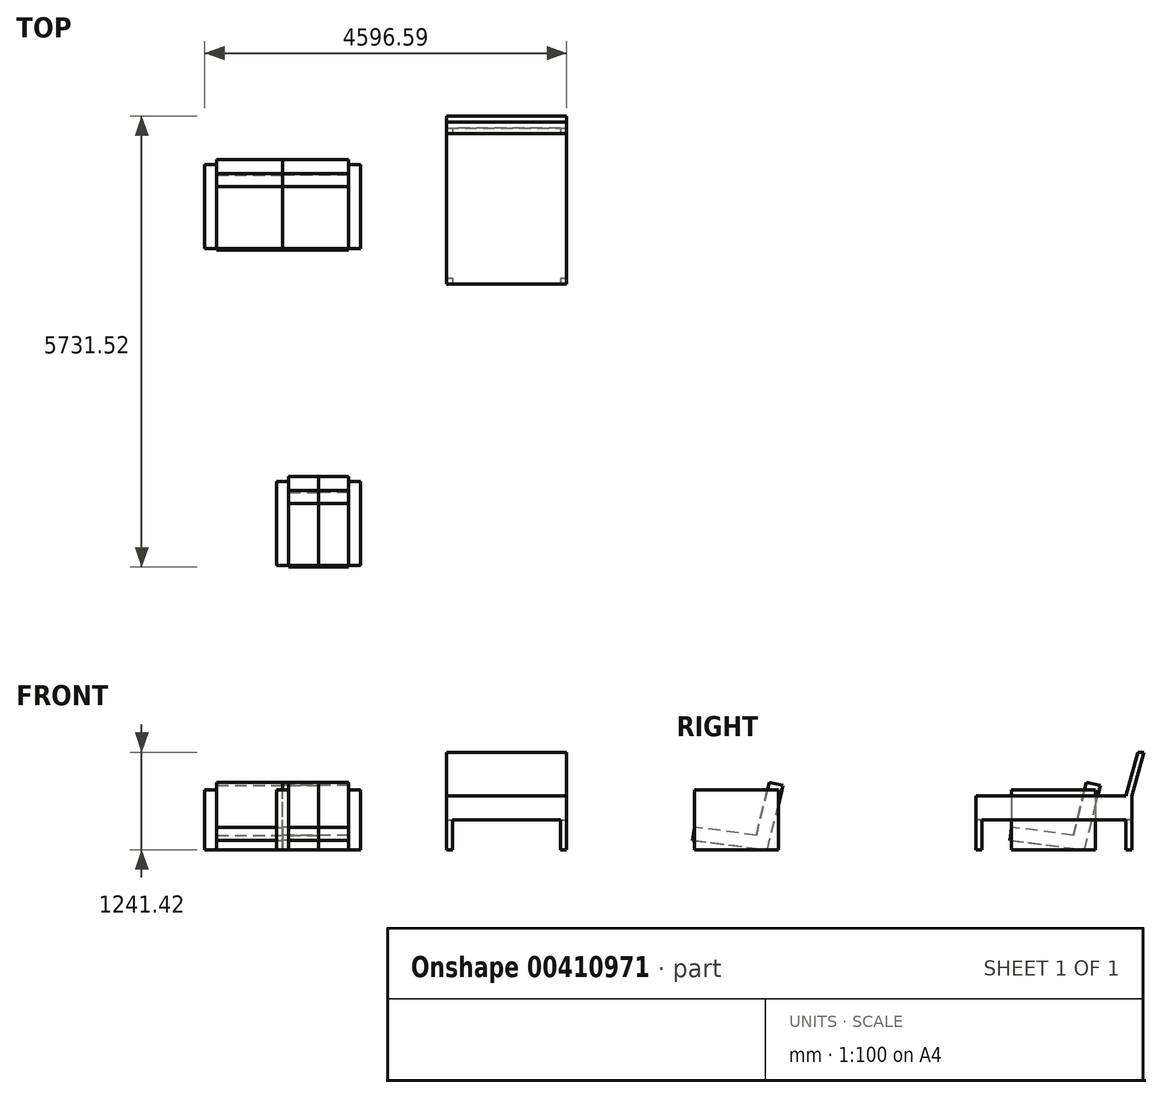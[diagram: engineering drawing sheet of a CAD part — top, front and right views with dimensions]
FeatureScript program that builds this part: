
annotation { "Feature Type Name" : "Feature", "Feature Type Description" : "" }
export const myFeature = defineFeature(function(context is Context, id is Id, definition is map)
    precondition{}
    {
        {
            var Q0;
            Q0=qCreatedBy(makeId("Top.planeOp"),FACE);
            var sketch = newSketch(context, id + "F0", { "sketchPlane" : qUnion([Q0])});
            skLineSegment(sketch, "E0.bottom", {"start": v(0, 0) * mm, "end": v(1524, 0) * mm});
            skLineSegment(sketch, "E0.top", {"start": v(0, 1981.2) * mm, "end": v(1524, 1981.2) * mm});
            skLineSegment(sketch, "E0.left", {"start": v(0, 0) * mm, "end": v(0, 1981.2) * mm});
            skLineSegment(sketch, "E0.right", {"start": v(1524, 0) * mm, "end": v(1524, 1981.2) * mm});
            skSolve(sketch);
        }
        {
            var Q0;
            Q0=makeQuery(id+"F0.imprint","IMPRINT",FACE,{"disambiguationData":[TD([[makeQuery(id+"F0.imprint","IMPRINT",EDGE,{"derivedFrom":sQuery(id+"F0.wireOp",EDGE,"E0.bottom")}),1.0]])]});
            extrude(context, id + "F1", {"entities" : qUnion([Q0]), "depth" : 685.8 * mm});
        }
        {
            var Q0;
            Q0=makeQuery(id+"F1.opExtrude","SWEPT_FACE",FACE,{"disambiguationData":[OSD([sQuery(id+"F0.wireOp",EDGE,"E0.bottom")])]});
            var sketch = newSketch(context, id + "F2", { "sketchPlane" : qUnion([Q0])});
            skLineSegment(sketch, "E1", {"start": v(0, 0) * mm, "end": v(76.2, 0) * mm});
            skLineSegment(sketch, "E2", {"start": v(76.2, 0) * mm, "end": v(76.2, 381) * mm});
            skLineSegment(sketch, "E3", {"start": v(76.2, 381) * mm, "end": v(1447.8, 381) * mm});
            skLineSegment(sketch, "E4", {"start": v(1447.8, 381) * mm, "end": v(1447.8, 0) * mm});
            skLineSegment(sketch, "E5", {"start": v(1447.8, 0) * mm, "end": v(1524, 0) * mm});
            skSolve(sketch);
        }
        {
            var Q0;
            {var subQ0=sQuery(id+"F2.wireOp",EDGE,"E2");Q0=makeQuery(id+"F2.imprint","IMPRINT",FACE,{"disambiguationData":[TD([[makeQuery(id+"F2.imprint","IMPRINT",EDGE,{"derivedFrom":subQ0}),-1.0]])]});}
            extrude(context, id + "F3", {"entities" : qUnion([Q0]), "operationType" : NewBodyOperationType.REMOVE, "endBound" : BoundingType.THROUGH_ALL, "oppositeDirection" : true, "depth" : 30.48 * mm});
        }
        {
            var Q0;
            Q0=makeQuery(id+"F1.opExtrude","SWEPT_FACE",FACE,{"disambiguationData":[OSD([sQuery(id+"F0.wireOp",EDGE,"E0.right")])]});
            var sketch = newSketch(context, id + "F4", { "sketchPlane" : qUnion([Q0])});
            skLineSegment(sketch, "E6", {"start": v(0, 0) * mm, "end": v(76.2, 0) * mm});
            skLineSegment(sketch, "E7", {"start": v(76.2, 0) * mm, "end": v(76.2, 381) * mm});
            skLineSegment(sketch, "E8", {"start": v(76.2, 381) * mm, "end": v(1905, 381) * mm});
            skLineSegment(sketch, "E9", {"start": v(1905, 381) * mm, "end": v(1905, 0) * mm});
            skLineSegment(sketch, "E10", {"start": v(1905, 0) * mm, "end": v(1981.2, 0) * mm});
            skSolve(sketch);
        }
        {
            var Q0;
            {var subQ0=sQuery(id+"F4.wireOp",EDGE,"E7");Q0=makeQuery(id+"F4.imprint","IMPRINT",FACE,{"disambiguationData":[TD([[makeQuery(id+"F4.imprint","IMPRINT",EDGE,{"derivedFrom":subQ0}),-1.0]])]});}
            extrude(context, id + "F5", {"entities" : qUnion([Q0]), "operationType" : NewBodyOperationType.REMOVE, "endBound" : BoundingType.THROUGH_ALL, "oppositeDirection" : true, "depth" : 30.48 * mm});
        }
        {
            var Q0;
            Q0=makeQuery(id+"F1.opExtrude","SWEPT_FACE",FACE,{"disambiguationData":[OSD([sQuery(id+"F0.wireOp",EDGE,"E0.right")])]});
            var sketch = newSketch(context, id + "F6", { "sketchPlane" : qUnion([Q0])});
            skLineSegment(sketch, "E11", {"start": v(1981.2, 685.8) * mm, "end": v(1906.52, 685.8) * mm});
            skLineSegment(sketch, "E12", {"start": v(1906.52, 685.8) * mm, "end": v(2057.29, 1241.42) * mm});
            skLineSegment(sketch, "E13", {"start": v(2057.29, 1241.42) * mm, "end": v(2131.97, 1241.42) * mm});
            skLineSegment(sketch, "E14", {"start": v(2131.97, 1241.42) * mm, "end": v(1981.2, 685.8) * mm});
            skSolve(sketch);
        }
        {
            var Q0;
            Q0=makeQuery(id+"F6.imprint","IMPRINT",FACE,{"disambiguationData":[TD([[makeQuery(id+"F6.imprint","IMPRINT",EDGE,{"derivedFrom":sQuery(id+"F6.wireOp",EDGE,"E11")}),1.0]])]});
            var Q1;
            Q1=makeQuery(id+"F1.opExtrude","SWEPT_FACE",FACE,{"disambiguationData":[OSD([sQuery(id+"F0.wireOp",EDGE,"E0.left")])]});
            extrude(context, id + "F7", {"entities" : qUnion([Q0]), "operationType" : NewBodyOperationType.ADD, "endBound" : BoundingType.UP_TO_SURFACE, "oppositeDirection" : true, "endBoundEntityFace" : qUnion([Q1]), "depth" : 30.48 * mm});
        }
        {
            var Q0;
            Q0=qCreatedBy(makeId("Top.planeOp"),FACE);
            var sketch = newSketch(context, id + "F8", { "sketchPlane" : qUnion([Q0])});
            skLineSegment(sketch, "E15.bottom", {"start": v(-2081.99, 1518) * mm, "end": v(-1091.39, 1518) * mm});
            skLineSegment(sketch, "E15.top", {"start": v(-2081.99, 451.2) * mm, "end": v(-1091.39, 451.2) * mm});
            skLineSegment(sketch, "E15.left", {"start": v(-2081.99, 1518) * mm, "end": v(-2081.99, 451.2) * mm});
            skLineSegment(sketch, "E15.right", {"start": v(-1091.39, 1518) * mm, "end": v(-1091.39, 451.2) * mm});
            skSolve(sketch);
        }
        {
            var Q0;
            Q0=makeQuery(id+"F8.imprint","IMPRINT",FACE,{"disambiguationData":[TD([[makeQuery(id+"F8.imprint","IMPRINT",EDGE,{"derivedFrom":sQuery(id+"F8.wireOp",EDGE,"E15.bottom")}),-1.0]])]});
            extrude(context, id + "F9", {"entities" : qUnion([Q0]), "depth" : 762 * mm});
        }
        {
            var Q0;
            Q0=makeQuery(id+"F9.opExtrude","SWEPT_FACE",FACE,{"disambiguationData":[OSD([sQuery(id+"F8.wireOp",EDGE,"E15.left")])]});
            var sketch = newSketch(context, id + "F10", { "sketchPlane" : qUnion([Q0])});
            skLineSegment(sketch, "E16", {"start": v(-1518, 762) * mm, "end": v(-1379.04, 762) * mm});
            skLineSegment(sketch, "E17", {"start": v(-1379.04, 762) * mm, "end": v(-1237.68, 187.2) * mm});
            skLineSegment(sketch, "E18", {"start": v(-1237.68, 187.2) * mm, "end": v(-451.2, 287.82) * mm});
            skLineSegment(sketch, "E19", {"start": v(-451.2, 287.82) * mm, "end": v(-451.2, 118.7) * mm});
            skLineSegment(sketch, "E20", {"start": v(-429.9, 121.43) * mm, "end": v(-1379.04, 0) * mm});
            skLineSegment(sketch, "E21", {"start": v(-1379.04, 0) * mm, "end": v(-1579.76, 816.14) * mm});
            skLineSegment(sketch, "E22", {"start": v(-1379.04, 762) * mm, "end": v(-1403.04, 859.6) * mm});
            skLineSegment(sketch, "E23", {"start": v(-1403.04, 859.6) * mm, "end": v(-1579.76, 816.14) * mm});
            skLineSegment(sketch, "E24", {"start": v(-451.2, 287.82) * mm, "end": v(-429.9, 121.43) * mm});
            skSolve(sketch);
        }
        {
            var Q0;
            {var subQ4=sQuery(id+"F10.wireOp",EDGE,"E16");Q0=makeQuery(id+"F10.imprint","IMPRINT",FACE,{"disambiguationData":[TD([[makeQuery(id+"F10.imprint","IMPRINT",EDGE,{"derivedFrom":subQ4}),1.0]])]});}
            var Q1;
            {var subQ0=sQuery(id+"F10.wireOp",EDGE,"E19");Q1=makeQuery(id+"F10.imprint","IMPRINT",FACE,{"disambiguationData":[TD([[makeQuery(id+"F10.imprint","IMPRINT",EDGE,{"derivedFrom":subQ0}),1.0]])]});}
            extrude(context, id + "F11", {"entities" : qUnion([Q0, Q1]), "operationType" : NewBodyOperationType.ADD, "oppositeDirection" : true, "depth" : 838.2 * mm});
        }
        {
            var Q0;
            {var subQ0=sQuery(id+"F8.wireOp",EDGE,"E15.left");Q0=makeQuery(id+"F11.boolean.opBoolean","MERGE",FACE,{"derivedFrom":[makeQuery(id+"F9.opExtrude","SWEPT_FACE",FACE,{"disambiguationData":[OSD([subQ0])]}),makeQuery(id+"F11.opExtrude","CAP_FACE",FACE,{"disambiguationData":[OSD([sQuery(id+"F8.wireOp",EDGE,"E15.bottom"),subQ0,sQuery(id+"F10.wireOp",EDGE,"E16"),sQuery(id+"F10.wireOp",EDGE,"E21"),sQuery(id+"F10.wireOp",EDGE,"E22"),sQuery(id+"F10.wireOp",EDGE,"E23")])],"isStart":true}),makeQuery(id+"F11.opExtrude","CAP_FACE",FACE,{"disambiguationData":[OSD([sQuery(id+"F10.wireOp",EDGE,"E19"),sQuery(id+"F10.wireOp",EDGE,"E20"),sQuery(id+"F10.wireOp",EDGE,"E24")])],"isStart":true})]});}
            var sketch = newSketch(context, id + "F12", { "sketchPlane" : qUnion([Q0])});
            skLineSegment(sketch, "E25", {"start": v(-1379.04, 762) * mm, "end": v(-1237.68, 187.2) * mm});
            skLineSegment(sketch, "E26", {"start": v(-1237.68, 187.2) * mm, "end": v(-451.2, 287.82) * mm});
            skLineSegment(sketch, "E27", {"start": v(-451.2, 287.82) * mm, "end": v(-451.2, 118.7) * mm});
            skLineSegment(sketch, "E28", {"start": v(-429.9, 121.43) * mm, "end": v(-1379.04, 0) * mm});
            skLineSegment(sketch, "E29", {"start": v(-1379.04, 0) * mm, "end": v(-1579.76, 816.14) * mm});
            skLineSegment(sketch, "E30", {"start": v(-1379.04, 762) * mm, "end": v(-1403.04, 859.6) * mm});
            skLineSegment(sketch, "E31", {"start": v(-1403.04, 859.6) * mm, "end": v(-1579.76, 816.14) * mm});
            skLineSegment(sketch, "E32", {"start": v(-451.2, 287.82) * mm, "end": v(-429.9, 121.43) * mm});
            skSolve(sketch);
        }
        {
            var Q0;
            Q0=makeQuery(id+"F12.imprint","IMPRINT",FACE,{"disambiguationData":[TD([[makeQuery(id+"F12.imprint","IMPRINT",EDGE,{"derivedFrom":sQuery(id+"F12.wireOp",EDGE,"E25")}),1.0]])]});
            var Q1;
            {var subQ1=sQuery(id+"F8.wireOp",EDGE,"E15.left");var subQ2=makeQuery(id+"F9.opExtrude","SWEPT_EDGE",EDGE,{"disambiguationData":[OSD([sQuery(id+"F8.wireOp",EDGE,"E15.bottom"),subQ1])]});Q1=makeQuery(id+"F12.imprint","IMPRINT",FACE,{"disambiguationData":[TD([[makeQuery(id+"F12.imprint","IMPRINT",EDGE,{"derivedFrom":subQ2}),1.0]])]});}
            var Q2;
            {var subQ1=sQuery(id+"F8.wireOp",EDGE,"E15.left");var subQ3=sQuery(id+"F8.wireOp",EDGE,"E15.top");var subQ4=sQuery(id+"F10.wireOp",EDGE,"E20");var subQ5=makeQuery(id+"F11.boolean.opBoolean","SPLIT",EDGE,{"disambiguationData":[TD([makeQuery(id+"F11.opExtrude","SWEPT_FACE",FACE,{"disambiguationData":[OSD([subQ4])]})])],"derivedFrom":makeQuery(id+"F9.opExtrude","SWEPT_EDGE",EDGE,{"disambiguationData":[OSD([subQ3,subQ1])]})});Q2=makeQuery(id+"F12.imprint","IMPRINT",FACE,{"disambiguationData":[TD([[makeQuery(id+"F12.imprint","IMPRINT",EDGE,{"derivedFrom":subQ5}),-1.0]])]});}
            extrude(context, id + "F13", {"entities" : qUnion([Q0, Q1, Q2]), "operationType" : NewBodyOperationType.REMOVE, "oppositeDirection" : true, "depth" : 838.2 * mm});
        }
        {
            var Q0;
            Q0=makeQuery(id+"F9.opExtrude","SWEPT_BODY",BODY,{"disambiguationData":[OSD([sQuery(id+"F8.wireOp",EDGE,"E15.bottom"),sQuery(id+"F8.wireOp",EDGE,"E15.top"),sQuery(id+"F8.wireOp",EDGE,"E15.left"),sQuery(id+"F8.wireOp",EDGE,"E15.right")])]});
            transform(context, id + "F14", {"entities" : qUnion([Q0]), "transformType" : TransformType.TRANSLATION_3D, "dx" : 0 * mm, "dy" : -4029.46 * mm, "dz" : 0 * mm, "makeCopy" : true});
        }
        {
            var Q0;
            {var subQ0=sQuery(id+"F8.wireOp",EDGE,"E15.left");Q0=makeQuery(id+"F14.opPattern","COPY",FACE,{"derivedFrom":makeQuery(id+"F11.boolean.opBoolean","MERGE",FACE,{"derivedFrom":[makeQuery(id+"F9.opExtrude","SWEPT_FACE",FACE,{"disambiguationData":[OSD([subQ0])]}),makeQuery(id+"F11.opExtrude","CAP_FACE",FACE,{"disambiguationData":[OSD([sQuery(id+"F8.wireOp",EDGE,"E15.bottom"),subQ0,sQuery(id+"F10.wireOp",EDGE,"E16"),sQuery(id+"F10.wireOp",EDGE,"E21"),sQuery(id+"F10.wireOp",EDGE,"E22"),sQuery(id+"F10.wireOp",EDGE,"E23")])],"isStart":true}),makeQuery(id+"F11.opExtrude","CAP_FACE",FACE,{"disambiguationData":[OSD([sQuery(id+"F10.wireOp",EDGE,"E19"),sQuery(id+"F10.wireOp",EDGE,"E20"),sQuery(id+"F10.wireOp",EDGE,"E24")])],"isStart":true})]}),"instanceName":"1"});}
            extrude(context, id + "F15", {"entities" : qUnion([Q0]), "operationType" : NewBodyOperationType.REMOVE, "oppositeDirection" : true, "depth" : 457.2 * mm});
        }
        {
            var Q0;
            Q0=makeQuery(id+"F9.opExtrude","SWEPT_BODY",BODY,{"disambiguationData":[OSD([sQuery(id+"F8.wireOp",EDGE,"E15.bottom"),sQuery(id+"F8.wireOp",EDGE,"E15.top"),sQuery(id+"F8.wireOp",EDGE,"E15.left"),sQuery(id+"F8.wireOp",EDGE,"E15.right")])]});
            var Q1;
            {var subQ0=sQuery(id+"F8.wireOp",EDGE,"E15.left");Q1=makeQuery(id+"F11.boolean.opBoolean","MERGE",FACE,{"derivedFrom":[makeQuery(id+"F9.opExtrude","SWEPT_FACE",FACE,{"disambiguationData":[OSD([subQ0])]}),makeQuery(id+"F11.opExtrude","CAP_FACE",FACE,{"disambiguationData":[OSD([sQuery(id+"F8.wireOp",EDGE,"E15.bottom"),subQ0,sQuery(id+"F10.wireOp",EDGE,"E16"),sQuery(id+"F10.wireOp",EDGE,"E21"),sQuery(id+"F10.wireOp",EDGE,"E22"),sQuery(id+"F10.wireOp",EDGE,"E23")])],"isStart":true}),makeQuery(id+"F11.opExtrude","CAP_FACE",FACE,{"disambiguationData":[OSD([sQuery(id+"F10.wireOp",EDGE,"E19"),sQuery(id+"F10.wireOp",EDGE,"E20"),sQuery(id+"F10.wireOp",EDGE,"E24")])],"isStart":true})]});}
            mirror(context, id + "F16", {"operationType" : NewBodyOperationType.ADD, "entities" : qUnion([Q0]), "mirrorPlane" : qUnion([Q1])});
        }
        {
            var Q0;
            Q0=makeQuery(id+"F14.opPattern","COPY",BODY,{"derivedFrom":makeQuery(id+"F9.opExtrude","SWEPT_BODY",BODY,{"disambiguationData":[OSD([sQuery(id+"F8.wireOp",EDGE,"E15.bottom"),sQuery(id+"F8.wireOp",EDGE,"E15.top"),sQuery(id+"F8.wireOp",EDGE,"E15.left"),sQuery(id+"F8.wireOp",EDGE,"E15.right")])]}),"instanceName":"1"});
            var Q1;
            Q1=makeQuery(id+"F15.boolean.opBoolean","COPY",FACE,{"derivedFrom":makeQuery(id+"F15.opExtrude","CAP_FACE",FACE,{"disambiguationData":[OSD([sQuery(id+"F8.wireOp",EDGE,"E15.bottom"),sQuery(id+"F8.wireOp",EDGE,"E15.left"),sQuery(id+"F10.wireOp",EDGE,"E16"),sQuery(id+"F10.wireOp",EDGE,"E19"),sQuery(id+"F10.wireOp",EDGE,"E20"),sQuery(id+"F10.wireOp",EDGE,"E21"),sQuery(id+"F10.wireOp",EDGE,"E22"),sQuery(id+"F10.wireOp",EDGE,"E23"),sQuery(id+"F10.wireOp",EDGE,"E24")])],"isStart":false})});
            mirror(context, id + "F17", {"operationType" : NewBodyOperationType.ADD, "entities" : qUnion([Q0]), "mirrorPlane" : qUnion([Q1])});
        }
    });
